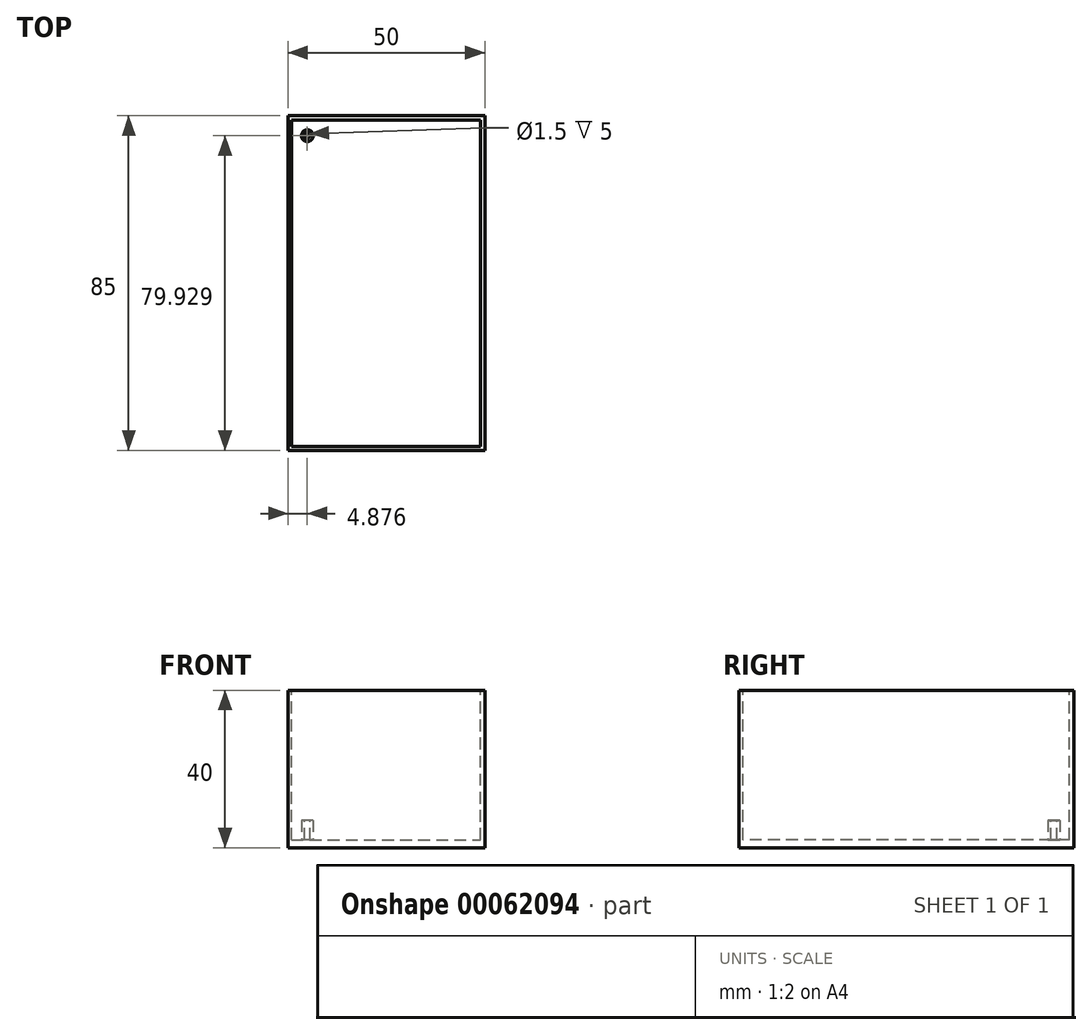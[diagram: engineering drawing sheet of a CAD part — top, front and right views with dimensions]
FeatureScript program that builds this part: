
annotation { "Feature Type Name" : "Feature", "Feature Type Description" : "" }
export const myFeature = defineFeature(function(context is Context, id is Id, definition is map)
    precondition{}
    {
        {
            var Q0;
            Q0=qCreatedBy(makeId("Top.planeOp"),FACE);
            var sketch = newSketch(context, id + "F0", { "sketchPlane" : qUnion([Q0])});
            skLineSegment(sketch, "E0.bottom", {"start": v(-34.94, 36.93) * mm, "end": v(15.06, 36.93) * mm});
            skLineSegment(sketch, "E0.top", {"start": v(-34.94, -48.07) * mm, "end": v(15.06, -48.07) * mm});
            skLineSegment(sketch, "E0.left", {"start": v(-34.94, 36.93) * mm, "end": v(-34.94, -48.07) * mm});
            skLineSegment(sketch, "E0.right", {"start": v(15.06, 36.93) * mm, "end": v(15.06, -48.07) * mm});
            skSolve(sketch);
        }
        {
            var Q0;
            Q0 = qSketchRegion(id + "F0", true);
            extrude(context, id + "F1", {"entities" : qUnion([Q0]), "depth" : 40 * mm});
        }
        {
            var Q0;
            Q0=makeQuery(id+"F1.opExtrude","CAP_FACE",FACE,{"disambiguationData":[OSD([sQuery(id+"F0.wireOp",EDGE,"E0.bottom"),sQuery(id+"F0.wireOp",EDGE,"E0.top"),sQuery(id+"F0.wireOp",EDGE,"E0.left"),sQuery(id+"F0.wireOp",EDGE,"E0.right")])],"isStart":false});
            var sketch = newSketch(context, id + "F2", { "sketchPlane" : qUnion([Q0])});
            skLineSegment(sketch, "E1.bottom", {"start": v(-34.06, 35.86) * mm, "end": v(13.94, 35.86) * mm});
            skLineSegment(sketch, "E1.top", {"start": v(-34.06, -47.14) * mm, "end": v(13.94, -47.14) * mm});
            skLineSegment(sketch, "E1.left", {"start": v(-34.06, 35.86) * mm, "end": v(-34.06, -47.14) * mm});
            skLineSegment(sketch, "E1.right", {"start": v(13.94, 35.86) * mm, "end": v(13.94, -47.14) * mm});
            skSolve(sketch);
        }
        {
            var Q0;
            Q0 = qSketchRegion(id + "F2", true);
            extrude(context, id + "F3", {"entities" : qUnion([Q0]), "operationType" : NewBodyOperationType.REMOVE, "oppositeDirection" : true, "depth" : 38 * mm});
        }
        {
            var Q0;
            Q0=makeQuery(id+"F3.boolean.opBoolean","COPY",FACE,{"derivedFrom":makeQuery(id+"F3.opExtrude","CAP_FACE",FACE,{"disambiguationData":[OSD([sQuery(id+"F2.wireOp",EDGE,"E1.bottom"),sQuery(id+"F2.wireOp",EDGE,"E1.top"),sQuery(id+"F2.wireOp",EDGE,"E1.left"),sQuery(id+"F2.wireOp",EDGE,"E1.right")])],"isStart":false})});
            var sketch = newSketch(context, id + "F4", { "sketchPlane" : qUnion([Q0])});
            skCircle(sketch, "E2", {"center": v(-30.06, 31.86) * mm, "radius": 1.5 * mm});
            skLineSegment(sketch, "E3", {"start": v(-30.06, 31.86) * mm, "end": v(-30.06, 35.86) * mm});
            skLineSegment(sketch, "E4", {"start": v(-30.06, 31.86) * mm, "end": v(-34.06, 31.86) * mm});
            skSolve(sketch);
        }
        {
            var Q0;
            Q0=makeQuery(id+"F4.imprint","IMPRINT",FACE,{"disambiguationData":[TD([[makeQuery(id+"F4.imprint","IMPRINT",EDGE,{"derivedFrom":sQuery(id+"F4.wireOp",EDGE,"E2")}),1.0]])]});
            var Q1;
            Q1=sQuery(id+"F4.wireOp",EDGE,"E2");
            extrude(context, id + "F5", {"entities" : qUnion([Q0]), "operationType" : NewBodyOperationType.ADD, "surfaceEntities" : qUnion([Q1]), "depth" : 5 * mm});
        }
        {
            var Q0;
            Q0=makeQuery(id+"F5.opExtrude","CAP_FACE",FACE,{"disambiguationData":[OSD([sQuery(id+"F4.wireOp",EDGE,"E2")])],"isStart":false});
            var sketch = newSketch(context, id + "F6", { "sketchPlane" : qUnion([Q0])});
            skCircle(sketch, "E5", {"center": v(-30.06, 31.86) * mm, "radius": 0.75 * mm});
            skSolve(sketch);
        }
        {
            var Q0;
            Q0 = qSketchRegion(id + "F6", true);
            extrude(context, id + "F7", {"entities" : qUnion([Q0]), "operationType" : NewBodyOperationType.REMOVE, "oppositeDirection" : true, "depth" : 5 * mm});
        }
    });
